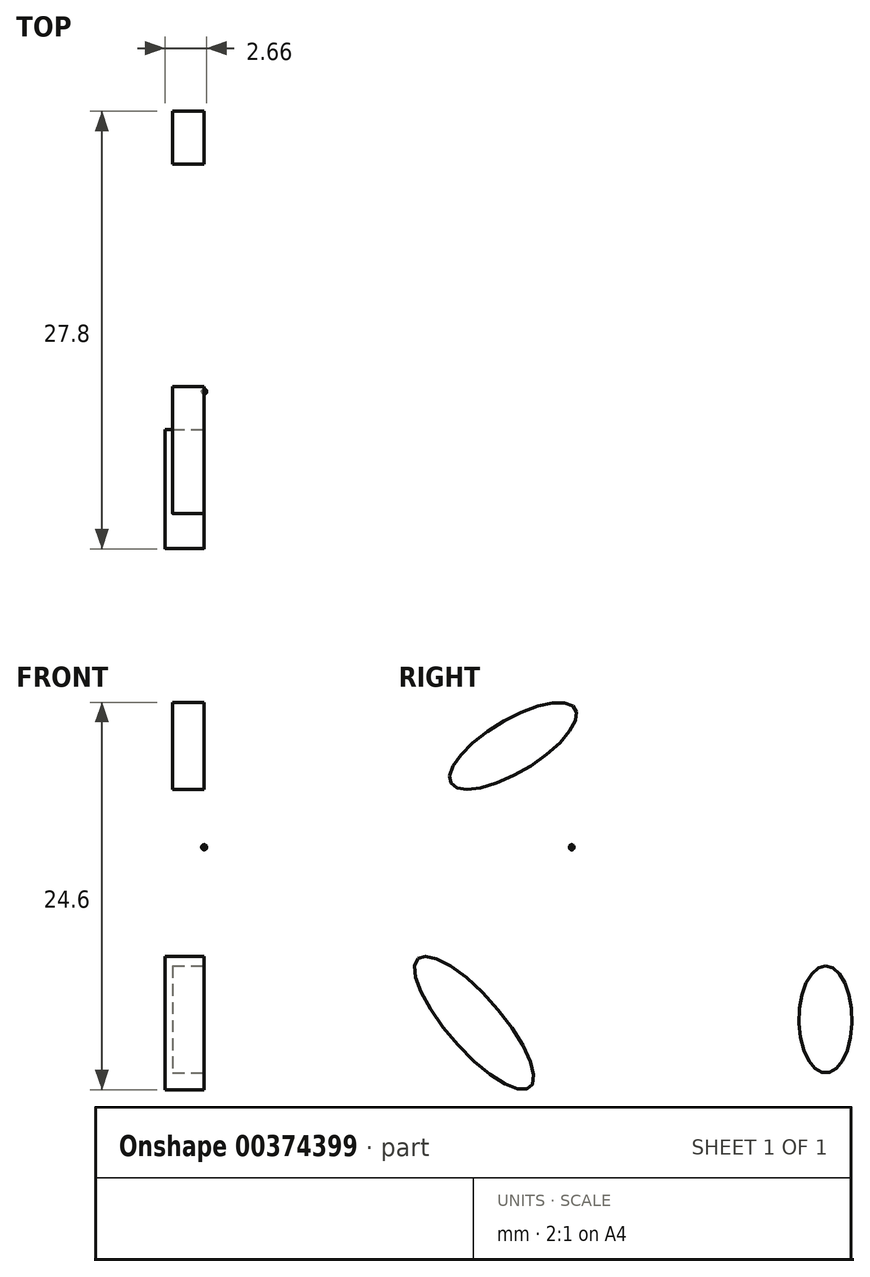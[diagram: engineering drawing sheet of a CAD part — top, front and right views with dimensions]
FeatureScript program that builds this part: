
annotation { "Feature Type Name" : "Feature", "Feature Type Description" : "" }
export const myFeature = defineFeature(function(context is Context, id is Id, definition is map)
    precondition{}
    {
        {
            var Q0;
            Q0=qCreatedBy(makeId("Front.planeOp"),FACE);
            var sketch = newSketch(context, id + "F0", { "sketchPlane" : qUnion([Q0])});
            skLineSegment(sketch, "E0", {"start": v(0, 0) * mm, "end": v(0, 20) * mm});
            skLineSegment(sketch, "E1", {"start": v(0, 0) * mm, "end": v(20.9, 0) * mm});
            skArc(sketch, "E2", {"start": v(20.9, 0) * mm, "mid": v(14.71, 14.46) * mm, "end": v(0, 20) * mm});
            skSolve(sketch);
        }
        {
            var Q0;
            Q0=makeQuery(id+"F0.imprint","IMPRINT",FACE,{"disambiguationData":[TD([[makeQuery(id+"F0.imprint","IMPRINT",EDGE,{"derivedFrom":sQuery(id+"F0.wireOp",EDGE,"E0")}),-1.0]])]});
            var Q1;
            Q1=sQuery(id+"F0.wireOp",EDGE,"E1");
            revolve(context, id + "F1", {"entities" : qUnion([Q0]), "axis" : qUnion([Q1]), "revolveType" : RevolveType.FULL});
        }
        {
            var Q0;
            Q0=qCreatedBy(makeId("Right.planeOp"),FACE);
            var sketch = newSketch(context, id + "F2", { "sketchPlane" : qUnion([Q0])});
            skLineSegment(sketch, "E3", {"start": v(0, 0) * mm, "end": v(0, 3) * mm});
            skLineSegment(sketch, "E4", {"start": v(0, 0) * mm, "end": v(-3, 0) * mm});
            skArc(sketch, "E5", {"start": v(0, 3) * mm, "mid": v(-2.14, 2.14) * mm, "end": v(-3, 0) * mm});
            skSolve(sketch);
        }
        {
            var Q0;
            Q0=qSketchRegion(id+"F2",true);
            var Q1;
            Q1=sQuery(id+"F2.wireOp",EDGE,"E4");
            revolve(context, id + "F3", {"operationType" : NewBodyOperationType.ADD, "entities" : qUnion([Q0]), "axis" : qUnion([Q1]), "revolveType" : RevolveType.FULL});
        }
        {
            var Q0;
            Q0=makeQuery(id+"F1.opRevolve","SWEPT_FACE",FACE,{"disambiguationData":[OSD([sQuery(id+"F0.wireOp",EDGE,"E0")])]});
            var sketch = newSketch(context, id + "F4", { "sketchPlane" : qUnion([Q0])});
            skLineSegment(sketch, "E6", {"start": v(0, 0) * mm, "end": v(-3, 0) * mm});
            skLineSegment(sketch, "E7", {"start": v(0, 0) * mm, "end": v(0, 3) * mm});
            skArc(sketch, "E8", {"start": v(0, 3) * mm, "mid": v(-2.1, 2.1) * mm, "end": v(-3, 0) * mm});
            skSolve(sketch);
        }
        {
            var Q0;
            Q0=makeQuery(id+"F4.imprint","IMPRINT",FACE,{"disambiguationData":[TD([[makeQuery(id+"F4.imprint","IMPRINT",EDGE,{"derivedFrom":sQuery(id+"F4.wireOp",EDGE,"E6")}),-1.0]])]});
            var Q1;
            Q1=sQuery(id+"F4.wireOp",EDGE,"E6");
            revolve(context, id + "F5", {"operationType" : NewBodyOperationType.ADD, "entities" : qUnion([Q0]), "axis" : qUnion([Q1]), "revolveType" : RevolveType.FULL});
        }
        {
            var Q0;
            Q0=makeQuery(id+"F1.opRevolve","SWEPT_FACE",FACE,{"disambiguationData":[OSD([sQuery(id+"F0.wireOp",EDGE,"E0")])]});
            var sketch = newSketch(context, id + "F6", { "sketchPlane" : qUnion([Q0])});
            skEllipse(sketch, "E9", {"center": v(9.46, -7.67) * mm, "majorRadius": 5.42 * mm, "minorRadius": 1.7 * mm, "majorAxis": v(0.66, 0.75)});
            skSolve(sketch);
        }
        {
            var Q0;
            Q0=qSketchRegion(id+"F6",true);
            extrude(context, id + "F7", {"entities" : qUnion([Q0]), "depth" : 2.5 * mm});
        }
        {
            var Q0;
            Q0=makeQuery(id+"F7.opExtrude","CAP_FACE",FACE,{"disambiguationData":[OSD([sQuery(id+"F6.wireOp",EDGE,"E9")])],"isStart":false});
            var sketch = newSketch(context, id + "F8", { "sketchPlane" : qUnion([Q0])});
            skFitSpline(sketch, "E10", {"points": [v(7.97, -11.28) * mm, v(6.8, -8.9) * mm, v(9.38, -10.19) * mm, v(8.17, -7.24) * mm, v(11, -8.49) * mm, v(9.27, -5.4) * mm, v(11.92, -6.7) * mm, v(11.05, -4) * mm, v(13.1, -5.01) * mm], "startDerivative": vector(-20.7, 30.85) * mm, "endDerivative": vector(27.66, -19.9) * mm});
            skSolve(sketch);
        }
        {
            var Q0;
            Q0=qSketchRegion(id+"F8",true);
            var Q1;
            Q1=sQuery(id+"F8.wireOp",EDGE,"E10");
            extrude(context, id + "F9", {"entities" : qUnion([Q0]), "bodyType" : ToolBodyType.SURFACE, "surfaceEntities" : qUnion([Q1]), "oppositeDirection" : true, "depth" : 2 * mm});
        }
        {
            var Q0;
            Q0=makeQuery(id+"F1.opRevolve","SWEPT_FACE",FACE,{"disambiguationData":[OSD([sQuery(id+"F0.wireOp",EDGE,"E0")])]});
            var sketch = newSketch(context, id + "F10", { "sketchPlane" : qUnion([Q0])});
            skSolve(sketch);
        }
        {
            var Q0;
            {var subQ1=sQuery(id+"F0.wireOp",EDGE,"E0");Q0=makeQuery(id+"F10.imprint","IMPRINT",FACE,{"disambiguationData":[TD([[makeQuery(id+"F10.imprint","IMPRINT",EDGE,{"derivedFrom":makeQuery(id+"F1.opRevolve","SWEPT_EDGE",EDGE,{"disambiguationData":[OSD([subQ1,sQuery(id+"F0.wireOp",EDGE,"E2")])]})}),1.0]])]});}
            var sketch = newSketch(context, id + "F11", { "sketchPlane" : qUnion([Q0])});
            skSolve(sketch);
        }
        {
            var Q0;
            {var subQ1=sQuery(id+"F0.wireOp",EDGE,"E0");Q0=makeQuery(id+"F10.imprint","IMPRINT",FACE,{"disambiguationData":[TD([[makeQuery(id+"F10.imprint","IMPRINT",EDGE,{"derivedFrom":makeQuery(id+"F1.opRevolve","SWEPT_EDGE",EDGE,{"disambiguationData":[OSD([subQ1,sQuery(id+"F0.wireOp",EDGE,"E2")])]})}),1.0]])]});}
            var sketch = newSketch(context, id + "F12", { "sketchPlane" : qUnion([Q0])});
            skEllipse(sketch, "E11", {"center": v(6.98, 9.93) * mm, "majorRadius": 4.6 * mm, "minorRadius": 1.66 * mm, "majorAxis": v(0.86, -0.51)});
            skSolve(sketch);
        }
        {
            var Q0;
            Q0=qSketchRegion(id+"F12",true);
            extrude(context, id + "F13", {"entities" : qUnion([Q0]), "depth" : 2 * mm});
        }
        {
            var Q0;
            Q0=makeQuery(id+"F13.opExtrude","CAP_FACE",FACE,{"disambiguationData":[OSD([sQuery(id+"F12.wireOp",EDGE,"E11")])],"isStart":false});
            var sketch = newSketch(context, id + "F14", { "sketchPlane" : qUnion([Q0])});
            skFitSpline(sketch, "E12", {"points": [v(4.68, 12.63) * mm, v(3.63, 10.54) * mm, v(6.2, 12.18) * mm, v(5.11, 9.18) * mm, v(7.84, 11.35) * mm, v(6.92, 8.06) * mm, v(9.45, 10.2) * mm, v(9.08, 7.26) * mm], "startDerivative": vector(-17.32, -26.87) * mm, "endDerivative": vector(-10.03, -33.63) * mm});
            skSolve(sketch);
        }
        {
            var Q0;
            Q0=qSketchRegion(id+"F14",true);
            var Q1;
            Q1=sQuery(id+"F14.wireOp",EDGE,"E12");
            extrude(context, id + "F15", {"entities" : qUnion([Q0]), "bodyType" : ToolBodyType.SURFACE, "surfaceEntities" : qUnion([Q1]), "oppositeDirection" : true, "depth" : 2 * mm});
        }
        {
            var Q0;
            {var subQ1=sQuery(id+"F0.wireOp",EDGE,"E0");Q0=makeQuery(id+"F10.imprint","IMPRINT",FACE,{"disambiguationData":[TD([[makeQuery(id+"F10.imprint","IMPRINT",EDGE,{"derivedFrom":makeQuery(id+"F1.opRevolve","SWEPT_EDGE",EDGE,{"disambiguationData":[OSD([subQ1,sQuery(id+"F0.wireOp",EDGE,"E2")])]})}),1.0]])]});}
            var sketch = newSketch(context, id + "F16", { "sketchPlane" : qUnion([Q0])});
            skFitSpline(sketch, "E13", {"points": [v(-13.4, 3.83) * mm, v(-13, 6.76) * mm, v(-11.02, 11.05) * mm, v(-7.06, 13.56) * mm, v(-3.83, 13.87) * mm, v(-2.72, 12.84) * mm, v(-4.78, 12.22) * mm, v(-7.76, 11.16) * mm, v(-9.8, 9.35) * mm, v(-10.94, 6.79) * mm, v(-11.41, 3.75) * mm, v(-10.83, 2.72) * mm, v(-9.4, 6.15) * mm, v(-7.32, 9.32) * mm, v(-3.78, 10.86) * mm, v(-3.25, 8.93) * mm, v(-5.3, 8.35) * mm, v(-7.26, 6.9) * mm, v(-8.35, 4.25) * mm, v(-7.57, 3.02) * mm, v(-6.48, 4.95) * mm, v(-5.4, 6.65) * mm, v(-2.94, 7.46) * mm, v(-2.5, 6.23) * mm, v(-4.8, 5.59) * mm, v(-6.14, 2.41) * mm], "startDerivative": vector(4.96, 65.1) * mm, "endDerivative": vector(-14.45, -88.75) * mm});
            skSolve(sketch);
        }
        {
            var Q0;
            Q0=qSketchRegion(id+"F16",true);
            var Q1;
            Q1=sQuery(id+"F16.wireOp",EDGE,"E13");
            extrude(context, id + "F17", {"entities" : qUnion([Q0]), "bodyType" : ToolBodyType.SURFACE, "surfaceEntities" : qUnion([Q1]), "depth" : 2 * mm});
        }
        {
            var Q0;
            {var subQ1=sQuery(id+"F0.wireOp",EDGE,"E0");Q0=makeQuery(id+"F10.imprint","IMPRINT",FACE,{"disambiguationData":[TD([[makeQuery(id+"F10.imprint","IMPRINT",EDGE,{"derivedFrom":makeQuery(id+"F1.opRevolve","SWEPT_EDGE",EDGE,{"disambiguationData":[OSD([subQ1,sQuery(id+"F0.wireOp",EDGE,"E2")])]})}),1.0]])]});}
            var sketch = newSketch(context, id + "F18", { "sketchPlane" : qUnion([Q0])});
            skFitSpline(sketch, "E14", {"points": [v(1.63, 7.11) * mm, v(4.78, 6.86) * mm, v(8.1, 5.2) * mm, v(9.66, 1.11) * mm, v(8.41, -3.01) * mm, v(4.67, -6.66) * mm, v(1.55, -7.21) * mm, v(1.07, -5.9) * mm, v(5.1, -4.45) * mm, v(7.63, -0.85) * mm, v(7.17, 3.33) * mm, v(4.59, 5.28) * mm, v(0, 5.94) * mm, v(0, 5.08) * mm, v(3.24, 4.42) * mm, v(5.82, 2.74) * mm, v(6.18, 0) * mm, v(5.56, -2.02) * mm, v(3.12, -3.79) * mm, v(1.15, -4.12) * mm, v(1.1, -3.42) * mm, v(3.12, -2.7) * mm, v(4.9, -0.76) * mm, v(4.7, 2.17) * mm, v(3.65, 3.54) * mm, v(1.42, 3.89) * mm, v(0, 3.94) * mm, v(0, 3.36) * mm, v(2.32, 3.19) * mm, v(3.68, 1.68) * mm, v(3.9, 0) * mm, v(3.27, -1.54) * mm, v(2.16, -2.36) * mm], "startDerivative": vector(88.94, -1.16) * mm, "endDerivative": vector(-52.62, -29.6) * mm});
            skSolve(sketch);
        }
        {
            var Q0;
            Q0=qSketchRegion(id+"F18",true);
            var Q1;
            Q1=sQuery(id+"F18.wireOp",EDGE,"E14");
            extrude(context, id + "F19", {"entities" : qUnion([Q0]), "bodyType" : ToolBodyType.SURFACE, "surfaceEntities" : qUnion([Q1]), "depth" : 1.8 * mm});
        }
        {
            var Q0;
            {var subQ1=sQuery(id+"F0.wireOp",EDGE,"E0");Q0=makeQuery(id+"F10.imprint","IMPRINT",FACE,{"disambiguationData":[TD([[makeQuery(id+"F10.imprint","IMPRINT",EDGE,{"derivedFrom":makeQuery(id+"F1.opRevolve","SWEPT_EDGE",EDGE,{"disambiguationData":[OSD([subQ1,sQuery(id+"F0.wireOp",EDGE,"E2")])]})}),1.0]])]});}
            var sketch = newSketch(context, id + "F20", { "sketchPlane" : qUnion([Q0])});
            skLineSegment(sketch, "E15", {"start": v(-7.66, -5.18) * mm, "end": v(-7.66, -3.88) * mm});
            skArc(sketch, "E16", {"start": v(-7.66, -3.88) * mm, "mid": v(-8.27, -4.53) * mm, "end": v(-7.66, -5.18) * mm});
            skSolve(sketch);
        }
        {
            var Q0;
            Q0=qSketchRegion(id+"F20",true);
            var Q1;
            Q1=sQuery(id+"F20.wireOp",EDGE,"E15");
            revolve(context, id + "F21", {"operationType" : NewBodyOperationType.ADD, "entities" : qUnion([Q0]), "axis" : qUnion([Q1]), "revolveType" : RevolveType.FULL});
        }
        {
            var Q0;
            {var subQ1=sQuery(id+"F0.wireOp",EDGE,"E0");Q0=makeQuery(id+"F10.imprint","IMPRINT",FACE,{"disambiguationData":[TD([[makeQuery(id+"F10.imprint","IMPRINT",EDGE,{"derivedFrom":makeQuery(id+"F1.opRevolve","SWEPT_EDGE",EDGE,{"disambiguationData":[OSD([subQ1,sQuery(id+"F0.wireOp",EDGE,"E2")])]})}),1.0]])]});}
            var sketch = newSketch(context, id + "F22", { "sketchPlane" : qUnion([Q0])});
            skLineSegment(sketch, "E17", {"start": v(12.74, 4.08) * mm, "end": v(12.74, 5.23) * mm});
            skArc(sketch, "E18", {"start": v(12.74, 5.23) * mm, "mid": v(12.17, 4.66) * mm, "end": v(12.74, 4.08) * mm});
            skSolve(sketch);
        }
        {
            var Q0;
            Q0=qSketchRegion(id+"F22",true);
            var Q1;
            Q1=sQuery(id+"F22.wireOp",EDGE,"E17");
            revolve(context, id + "F23", {"operationType" : NewBodyOperationType.ADD, "entities" : qUnion([Q0]), "axis" : qUnion([Q1]), "revolveType" : RevolveType.FULL});
        }
        {
            var Q0;
            {var subQ1=sQuery(id+"F0.wireOp",EDGE,"E0");Q0=makeQuery(id+"F10.imprint","IMPRINT",FACE,{"disambiguationData":[TD([[makeQuery(id+"F10.imprint","IMPRINT",EDGE,{"derivedFrom":makeQuery(id+"F1.opRevolve","SWEPT_EDGE",EDGE,{"disambiguationData":[OSD([subQ1,sQuery(id+"F0.wireOp",EDGE,"E2")])]})}),1.0]])]});}
            var sketch = newSketch(context, id + "F24", { "sketchPlane" : qUnion([Q0])});
            skLineSegment(sketch, "E19", {"start": v(-5.97, -14.13) * mm, "end": v(-5.97, -12.52) * mm});
            skArc(sketch, "E20", {"start": v(-5.97, -12.52) * mm, "mid": v(-6.78, -13.33) * mm, "end": v(-5.97, -14.13) * mm});
            skSolve(sketch);
        }
        {
            var Q0;
            Q0=qSketchRegion(id+"F24",true);
            var Q1;
            Q1=sQuery(id+"F24.wireOp",EDGE,"E19");
            revolve(context, id + "F25", {"operationType" : NewBodyOperationType.ADD, "entities" : qUnion([Q0]), "axis" : qUnion([Q1]), "revolveType" : RevolveType.FULL});
        }
        {
            var Q0;
            {var subQ1=sQuery(id+"F0.wireOp",EDGE,"E0");Q0=makeQuery(id+"F10.imprint","IMPRINT",FACE,{"disambiguationData":[TD([[makeQuery(id+"F10.imprint","IMPRINT",EDGE,{"derivedFrom":makeQuery(id+"F1.opRevolve","SWEPT_EDGE",EDGE,{"disambiguationData":[OSD([subQ1,sQuery(id+"F0.wireOp",EDGE,"E2")])]})}),1.0]])]});}
            var sketch = newSketch(context, id + "F26", { "sketchPlane" : qUnion([Q0])});
            skLineSegment(sketch, "E21", {"start": v(-3.75, 16.1) * mm, "end": v(-2.67, 17.25) * mm});
            skArc(sketch, "E22", {"start": v(-2.67, 17.25) * mm, "mid": v(-3.8, 17.24) * mm, "end": v(-3.75, 16.1) * mm});
            skSolve(sketch);
        }
        {
            var Q0;
            Q0=qSketchRegion(id+"F26",true);
            var Q1;
            Q1=sQuery(id+"F26.wireOp",EDGE,"E21");
            revolve(context, id + "F27", {"operationType" : NewBodyOperationType.ADD, "entities" : qUnion([Q0]), "axis" : qUnion([Q1]), "revolveType" : RevolveType.FULL});
        }
        {
            var Q0;
            {var subQ1=sQuery(id+"F0.wireOp",EDGE,"E0");Q0=makeQuery(id+"F10.imprint","IMPRINT",FACE,{"disambiguationData":[TD([[makeQuery(id+"F10.imprint","IMPRINT",EDGE,{"derivedFrom":makeQuery(id+"F1.opRevolve","SWEPT_EDGE",EDGE,{"disambiguationData":[OSD([subQ1,sQuery(id+"F0.wireOp",EDGE,"E2")])]})}),1.0]])]});}
            var sketch = newSketch(context, id + "F28", { "sketchPlane" : qUnion([Q0])});
            skLineSegment(sketch, "E23", {"start": v(3.12, 3.49) * mm, "end": v(3.4, 3.49) * mm});
            skArc(sketch, "E24", {"start": v(3.4, 3.49) * mm, "mid": v(3.26, 3.61) * mm, "end": v(3.12, 3.49) * mm});
            skSolve(sketch);
        }
        {
            var Q0;
            Q0=qSketchRegion(id+"F28",true);
            var Q1;
            Q1=sQuery(id+"F28.wireOp",EDGE,"E23");
            revolve(context, id + "F29", {"entities" : qUnion([Q0]), "axis" : qUnion([Q1]), "revolveType" : RevolveType.FULL});
        }
        {
            var Q0;
            {var subQ1=sQuery(id+"F0.wireOp",EDGE,"E0");Q0=makeQuery(id+"F10.imprint","IMPRINT",FACE,{"disambiguationData":[TD([[makeQuery(id+"F10.imprint","IMPRINT",EDGE,{"derivedFrom":makeQuery(id+"F1.opRevolve","SWEPT_EDGE",EDGE,{"disambiguationData":[OSD([subQ1,sQuery(id+"F0.wireOp",EDGE,"E2")])]})}),1.0]])]});}
            var sketch = newSketch(context, id + "F30", { "sketchPlane" : qUnion([Q0])});
            skLineSegment(sketch, "E25", {"start": v(1.66, 2.96) * mm, "end": v(2.07, 2.96) * mm});
            skArc(sketch, "E26", {"start": v(2.07, 2.96) * mm, "mid": v(1.86, 3.17) * mm, "end": v(1.66, 2.96) * mm});
            skSolve(sketch);
        }
        {
            var Q0;
            Q0=qSketchRegion(id+"F30",true);
            var Q1;
            Q1=sQuery(id+"F30.wireOp",EDGE,"E25");
            revolve(context, id + "F31", {"operationType" : NewBodyOperationType.ADD, "entities" : qUnion([Q0]), "axis" : qUnion([Q1]), "revolveType" : RevolveType.FULL});
        }
        {
            var Q0;
            {var subQ1=sQuery(id+"F0.wireOp",EDGE,"E0");Q0=makeQuery(id+"F10.imprint","IMPRINT",FACE,{"disambiguationData":[TD([[makeQuery(id+"F10.imprint","IMPRINT",EDGE,{"derivedFrom":makeQuery(id+"F1.opRevolve","SWEPT_EDGE",EDGE,{"disambiguationData":[OSD([subQ1,sQuery(id+"F0.wireOp",EDGE,"E2")])]})}),1.0]])]});}
            var sketch = newSketch(context, id + "F32", { "sketchPlane" : qUnion([Q0])});
            skLineSegment(sketch, "E27", {"start": v(4.55, 2) * mm, "end": v(4.73, 2) * mm});
            skArc(sketch, "E28", {"start": v(4.73, 2) * mm, "mid": v(4.64, 2.07) * mm, "end": v(4.55, 2) * mm});
            skSolve(sketch);
        }
        {
            var Q0;
            Q0=qSketchRegion(id+"F32",true);
            var Q1;
            Q1=sQuery(id+"F32.wireOp",EDGE,"E27");
            revolve(context, id + "F33", {"operationType" : NewBodyOperationType.ADD, "entities" : qUnion([Q0]), "axis" : qUnion([Q1]), "revolveType" : RevolveType.FULL});
        }
        {
            var Q0;
            {var subQ1=sQuery(id+"F0.wireOp",EDGE,"E0");Q0=makeQuery(id+"F10.imprint","IMPRINT",FACE,{"disambiguationData":[TD([[makeQuery(id+"F10.imprint","IMPRINT",EDGE,{"derivedFrom":makeQuery(id+"F1.opRevolve","SWEPT_EDGE",EDGE,{"disambiguationData":[OSD([subQ1,sQuery(id+"F0.wireOp",EDGE,"E2")])]})}),1.0]])]});}
            var sketch = newSketch(context, id + "F34", { "sketchPlane" : qUnion([Q0])});
            skLineSegment(sketch, "E29", {"start": v(4.5, -0.38) * mm, "end": v(4.7, -0.38) * mm});
            skArc(sketch, "E30", {"start": v(4.5, -0.38) * mm, "mid": v(4.6, -0.48) * mm, "end": v(4.7, -0.38) * mm});
            skSolve(sketch);
        }
        {
            var Q0;
            Q0=qSketchRegion(id+"F34",true);
            var Q1;
            Q1=sQuery(id+"F34.wireOp",EDGE,"E29");
            revolve(context, id + "F35", {"operationType" : NewBodyOperationType.ADD, "entities" : qUnion([Q0]), "axis" : qUnion([Q1]), "revolveType" : RevolveType.FULL});
        }
        {
            var Q0;
            {var subQ1=sQuery(id+"F0.wireOp",EDGE,"E0");Q0=makeQuery(id+"F10.imprint","IMPRINT",FACE,{"disambiguationData":[TD([[makeQuery(id+"F10.imprint","IMPRINT",EDGE,{"derivedFrom":makeQuery(id+"F1.opRevolve","SWEPT_EDGE",EDGE,{"disambiguationData":[OSD([subQ1,sQuery(id+"F0.wireOp",EDGE,"E2")])]})}),1.0]])]});}
            var sketch = newSketch(context, id + "F36", { "sketchPlane" : qUnion([Q0])});
            skLineSegment(sketch, "E31", {"start": v(2.2, -3.15) * mm, "end": v(2.49, -3.15) * mm});
            skArc(sketch, "E32", {"start": v(2.49, -3.15) * mm, "mid": v(2.34, -3) * mm, "end": v(2.2, -3.15) * mm});
            skSolve(sketch);
        }
        {
            var Q0;
            Q0=qSketchRegion(id+"F36",true);
            var Q1;
            Q1=sQuery(id+"F36.wireOp",EDGE,"E31");
            revolve(context, id + "F37", {"operationType" : NewBodyOperationType.ADD, "entities" : qUnion([Q0]), "axis" : qUnion([Q1]), "revolveType" : RevolveType.FULL});
        }
        {
            var Q0;
            {var subQ1=sQuery(id+"F0.wireOp",EDGE,"E0");Q0=makeQuery(id+"F10.imprint","IMPRINT",FACE,{"disambiguationData":[TD([[makeQuery(id+"F10.imprint","IMPRINT",EDGE,{"derivedFrom":makeQuery(id+"F1.opRevolve","SWEPT_EDGE",EDGE,{"disambiguationData":[OSD([subQ1,sQuery(id+"F0.wireOp",EDGE,"E2")])]})}),1.0]])]});}
            var sketch = newSketch(context, id + "F38", { "sketchPlane" : qUnion([Q0])});
            skLineSegment(sketch, "E33", {"start": v(3.6, 0.96) * mm, "end": v(3.78, 0.96) * mm});
            skArc(sketch, "E34", {"start": v(3.78, 0.96) * mm, "mid": v(3.7, 1.05) * mm, "end": v(3.6, 0.96) * mm});
            skSolve(sketch);
        }
        {
            var Q0;
            Q0=qSketchRegion(id+"F38",true);
            var Q1;
            Q1=sQuery(id+"F38.wireOp",EDGE,"E33");
            revolve(context, id + "F39", {"operationType" : NewBodyOperationType.ADD, "entities" : qUnion([Q0]), "axis" : qUnion([Q1]), "revolveType" : RevolveType.FULL});
        }
        {
            var Q0;
            {var subQ1=sQuery(id+"F0.wireOp",EDGE,"E0");Q0=makeQuery(id+"F10.imprint","IMPRINT",FACE,{"disambiguationData":[TD([[makeQuery(id+"F10.imprint","IMPRINT",EDGE,{"derivedFrom":makeQuery(id+"F1.opRevolve","SWEPT_EDGE",EDGE,{"disambiguationData":[OSD([subQ1,sQuery(id+"F0.wireOp",EDGE,"E2")])]})}),1.0]])]});}
            var sketch = newSketch(context, id + "F40", { "sketchPlane" : qUnion([Q0])});
            skLineSegment(sketch, "E35", {"start": v(0.35, 3.91) * mm, "end": v(0.56, 3.91) * mm});
            skArc(sketch, "E36", {"start": v(0.56, 3.91) * mm, "mid": v(0.46, 4.02) * mm, "end": v(0.35, 3.91) * mm});
            skSolve(sketch);
        }
        {
            var Q0;
            Q0=qSketchRegion(id+"F40",true);
            var Q1;
            Q1=sQuery(id+"F40.wireOp",EDGE,"E35");
            revolve(context, id + "F41", {"operationType" : NewBodyOperationType.ADD, "entities" : qUnion([Q0]), "axis" : qUnion([Q1]), "revolveType" : RevolveType.FULL});
        }
        {
            var Q0;
            {var subQ1=sQuery(id+"F0.wireOp",EDGE,"E0");Q0=makeQuery(id+"F10.imprint","IMPRINT",FACE,{"disambiguationData":[TD([[makeQuery(id+"F10.imprint","IMPRINT",EDGE,{"derivedFrom":makeQuery(id+"F1.opRevolve","SWEPT_EDGE",EDGE,{"disambiguationData":[OSD([subQ1,sQuery(id+"F0.wireOp",EDGE,"E2")])]})}),1.0]])]});}
            var sketch = newSketch(context, id + "F42", { "sketchPlane" : qUnion([Q0])});
            skLineSegment(sketch, "E37", {"start": v(5.24, 1) * mm, "end": v(5.43, 0.8) * mm});
            skArc(sketch, "E38", {"start": v(5.43, 0.8) * mm, "mid": v(5.44, 1) * mm, "end": v(5.24, 1) * mm});
            skSolve(sketch);
        }
        {
            var Q0;
            Q0=qSketchRegion(id+"F42",true);
            var Q1;
            Q1=sQuery(id+"F42.wireOp",EDGE,"E37");
            revolve(context, id + "F43", {"operationType" : NewBodyOperationType.ADD, "entities" : qUnion([Q0]), "axis" : qUnion([Q1]), "revolveType" : RevolveType.FULL});
        }
        {
            var Q0;
            {var subQ1=sQuery(id+"F0.wireOp",EDGE,"E0");Q0=makeQuery(id+"F11.imprint","IMPRINT",FACE,{"disambiguationData":[TD([[makeQuery(id+"F11.imprint","IMPRINT",EDGE,{"derivedFrom":makeQuery(id+"F10.imprint","IMPRINT",EDGE,{"derivedFrom":makeQuery(id+"F1.opRevolve","SWEPT_EDGE",EDGE,{"disambiguationData":[OSD([subQ1,sQuery(id+"F0.wireOp",EDGE,"E2")])]})})}),1.0]])]});}
            var sketch = newSketch(context, id + "F44", { "sketchPlane" : qUnion([Q0])});
            skLineSegment(sketch, "E39", {"start": v(4.34, -2.15) * mm, "end": v(4.53, -1.94) * mm});
            skArc(sketch, "E40", {"start": v(4.53, -1.94) * mm, "mid": v(4.33, -1.95) * mm, "end": v(4.34, -2.15) * mm});
            skSolve(sketch);
        }
        {
            var Q0;
            Q0=qSketchRegion(id+"F44",true);
            var Q1;
            Q1=sQuery(id+"F44.wireOp",EDGE,"E39");
            revolve(context, id + "F45", {"operationType" : NewBodyOperationType.ADD, "entities" : qUnion([Q0]), "axis" : qUnion([Q1]), "revolveType" : RevolveType.FULL});
        }
        {
            var Q0;
            {var subQ1=sQuery(id+"F0.wireOp",EDGE,"E0");Q0=makeQuery(id+"F11.imprint","IMPRINT",FACE,{"disambiguationData":[TD([[makeQuery(id+"F11.imprint","IMPRINT",EDGE,{"derivedFrom":makeQuery(id+"F10.imprint","IMPRINT",EDGE,{"derivedFrom":makeQuery(id+"F1.opRevolve","SWEPT_EDGE",EDGE,{"disambiguationData":[OSD([subQ1,sQuery(id+"F0.wireOp",EDGE,"E2")])]})})}),1.0]])]});}
            var sketch = newSketch(context, id + "F46", { "sketchPlane" : qUnion([Q0])});
            skLineSegment(sketch, "E41", {"start": v(3.35, -1.58) * mm, "end": v(3.52, -1.58) * mm});
            skArc(sketch, "E42", {"start": v(3.35, -1.58) * mm, "mid": v(3.43, -1.67) * mm, "end": v(3.52, -1.58) * mm});
            skSolve(sketch);
        }
        {
            var Q0;
            Q0=qSketchRegion(id+"F46",true);
            var Q1;
            Q1=sQuery(id+"F46.wireOp",EDGE,"E41");
            revolve(context, id + "F47", {"operationType" : NewBodyOperationType.ADD, "entities" : qUnion([Q0]), "axis" : qUnion([Q1]), "revolveType" : RevolveType.FULL});
        }
        {
            var Q0;
            {var subQ1=sQuery(id+"F0.wireOp",EDGE,"E0");Q0=makeQuery(id+"F11.imprint","IMPRINT",FACE,{"disambiguationData":[TD([[makeQuery(id+"F11.imprint","IMPRINT",EDGE,{"derivedFrom":makeQuery(id+"F10.imprint","IMPRINT",EDGE,{"derivedFrom":makeQuery(id+"F1.opRevolve","SWEPT_EDGE",EDGE,{"disambiguationData":[OSD([subQ1,sQuery(id+"F0.wireOp",EDGE,"E2")])]})})}),1.0]])]});}
            var sketch = newSketch(context, id + "F48", { "sketchPlane" : qUnion([Q0])});
            skEllipse(sketch, "E43", {"center": v(-12.87, -7.45) * mm, "majorRadius": 3.4 * mm, "minorRadius": 1.69 * mm, "majorAxis": v(0, 1)});
            skSolve(sketch);
        }
        {
            var Q0;
            Q0=qSketchRegion(id+"F48",true);
            extrude(context, id + "F49", {"entities" : qUnion([Q0]), "depth" : 2 * mm});
        }
        {
            var Q0;
            Q0=makeQuery(id+"F49.opExtrude","CAP_FACE",FACE,{"disambiguationData":[OSD([sQuery(id+"F48.wireOp",EDGE,"E43")])],"isStart":false});
            var sketch = newSketch(context, id + "F50", { "sketchPlane" : qUnion([Q0])});
            skFitSpline(sketch, "E44", {"points": [v(-11.66, -9.82) * mm, v(-14.04, -9.89) * mm, v(-11.29, -8.66) * mm, v(-14.53, -7.96) * mm, v(-11.19, -7.13) * mm, v(-14.5, -6.55) * mm, v(-11.4, -5.75) * mm, v(-14.12, -5.2) * mm], "startDerivative": vector(-32.3, -3.08) * mm, "endDerivative": vector(-34.6, 3.54) * mm});
            skSolve(sketch);
        }
        {
            var Q0;
            Q0 = qSketchRegion(id + "F50", true);
            var Q1;
            Q1=sQuery(id+"F50.wireOp",EDGE,"E44");
            extrude(context, id + "F51", {"entities" : qUnion([Q0]), "bodyType" : ToolBodyType.SURFACE, "surfaceEntities" : qUnion([Q1]), "oppositeDirection" : true, "depth" : 2 * mm});
        }
        {
            var Q0;
            {var subQ1=sQuery(id+"F0.wireOp",EDGE,"E0");Q0=makeQuery(id+"F11.imprint","IMPRINT",FACE,{"disambiguationData":[TD([[makeQuery(id+"F11.imprint","IMPRINT",EDGE,{"derivedFrom":makeQuery(id+"F10.imprint","IMPRINT",EDGE,{"derivedFrom":makeQuery(id+"F1.opRevolve","SWEPT_EDGE",EDGE,{"disambiguationData":[OSD([subQ1,sQuery(id+"F0.wireOp",EDGE,"E2")])]})})}),1.0]])]});}
            var sketch = newSketch(context, id + "F52", { "sketchPlane" : qUnion([Q0])});
            skLineSegment(sketch, "E45", {"start": v(1.04, -10.79) * mm, "end": v(2.2, -10.79) * mm});
            skArc(sketch, "E46", {"start": v(2.2, -10.79) * mm, "mid": v(1.62, -10.22) * mm, "end": v(1.04, -10.79) * mm});
            skSolve(sketch);
        }
        {
            var Q0;
            Q0 = qSketchRegion(id + "F52", true);
            var Q1;
            Q1=sQuery(id+"F52.wireOp",EDGE,"E45");
            revolve(context, id + "F53", {"operationType" : NewBodyOperationType.ADD, "entities" : qUnion([Q0]), "axis" : qUnion([Q1]), "revolveType" : RevolveType.FULL});
        }
        {
            var Q0;
            {var subQ1=sQuery(id+"F0.wireOp",EDGE,"E0");Q0=makeQuery(id+"F11.imprint","IMPRINT",FACE,{"disambiguationData":[TD([[makeQuery(id+"F11.imprint","IMPRINT",EDGE,{"derivedFrom":makeQuery(id+"F10.imprint","IMPRINT",EDGE,{"derivedFrom":makeQuery(id+"F1.opRevolve","SWEPT_EDGE",EDGE,{"disambiguationData":[OSD([subQ1,sQuery(id+"F0.wireOp",EDGE,"E2")])]})})}),1.0]])]});}
            var sketch = newSketch(context, id + "F54", { "sketchPlane" : qUnion([Q0])});
            skCircle(sketch, "E47", {"center": v(2.2, -18.68) * mm, "radius": 0.6 * mm});
            skPoint(sketch, "E47.first.point", {"position": v(2.5, -18.15) * mm});
            skPoint(sketch, "E47.second.point", {"position": v(2.25, -19.28) * mm});
            skPoint(sketch, "E47.third.point", {"position": v(1.71, -18.3) * mm});
            skSolve(sketch);
        }
        {
            var Q0;
            Q0 = qSketchRegion(id + "F54", true);
            extrude(context, id + "F55", {"entities" : qUnion([Q0]), "operationType" : NewBodyOperationType.REMOVE, "depth" : 20 * mm});
        }
        {
            var Q0;
            {var subQ1=sQuery(id+"F0.wireOp",EDGE,"E0");Q0=makeQuery(id+"F11.imprint","IMPRINT",FACE,{"disambiguationData":[TD([[makeQuery(id+"F11.imprint","IMPRINT",EDGE,{"derivedFrom":makeQuery(id+"F10.imprint","IMPRINT",EDGE,{"derivedFrom":makeQuery(id+"F1.opRevolve","SWEPT_EDGE",EDGE,{"disambiguationData":[OSD([subQ1,sQuery(id+"F0.wireOp",EDGE,"E2")])]})})}),1.0]])]});}
            var sketch = newSketch(context, id + "F56", { "sketchPlane" : qUnion([Q0])});
            skCircle(sketch, "E48", {"center": v(2.91, -17.45) * mm, "radius": 1.08 * mm});
            skSolve(sketch);
        }
        {
            var Q0;
            Q0 = qSketchRegion(id + "F56", true);
            extrude(context, id + "F57", {"entities" : qUnion([Q0]), "operationType" : NewBodyOperationType.REMOVE, "oppositeDirection" : true, "depth" : 25 * mm});
        }
    });
